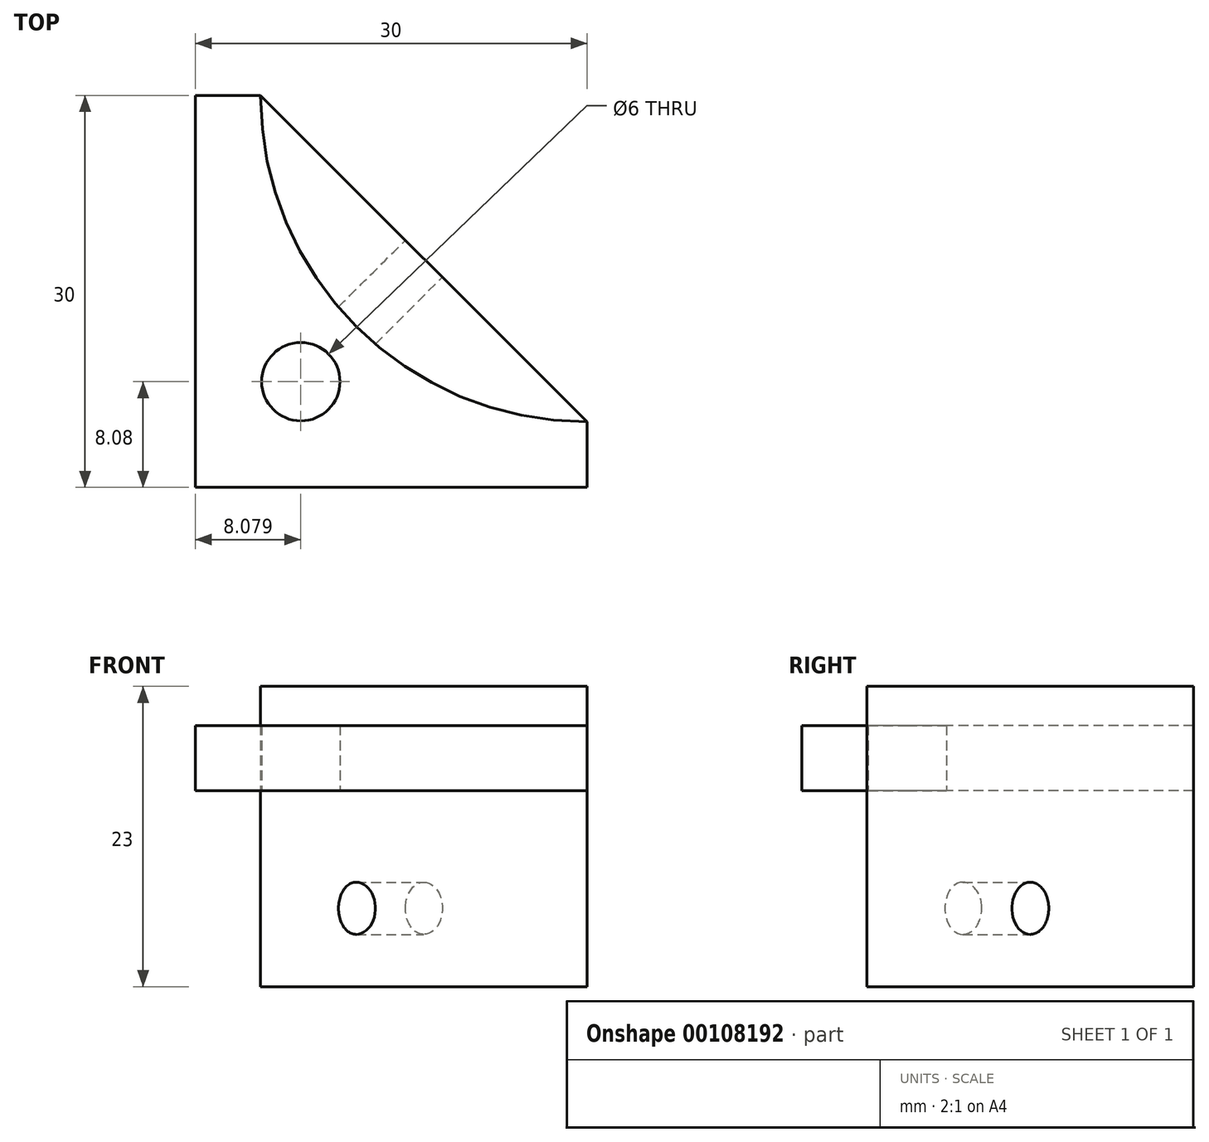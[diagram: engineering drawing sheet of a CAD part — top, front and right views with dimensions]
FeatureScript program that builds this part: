
annotation { "Feature Type Name" : "Feature", "Feature Type Description" : "" }
export const myFeature = defineFeature(function(context is Context, id is Id, definition is map)
    precondition{}
    {
        {
            var Q0;
            Q0=qCreatedBy(makeId("Top.planeOp"),FACE);
            var sketch = newSketch(context, id + "F0", { "sketchPlane" : qUnion([Q0])});
            skLineSegment(sketch, "E0.bottom", {"start": v(-30, 30) * mm, "end": v(30, 30) * mm});
            skLineSegment(sketch, "E0.top", {"start": v(-30, -30) * mm, "end": v(30, -30) * mm});
            skLineSegment(sketch, "E0.left", {"start": v(-30, 30) * mm, "end": v(-30, -30) * mm});
            skLineSegment(sketch, "E0.right", {"start": v(30, 30) * mm, "end": v(30, -30) * mm});
            skPoint(sketch, "E0.middle", {"position": v(0, 0) * mm});
            skCircle(sketch, "E1", {"center": v(0, 0) * mm, "radius": 25 * mm});
            skLineSegment(sketch, "E2", {"start": v(-30, 0) * mm, "end": v(-25, 0) * mm});
            skLineSegment(sketch, "E3", {"start": v(-25, 0) * mm, "end": v(0, -25) * mm});
            skLineSegment(sketch, "E4", {"start": v(0, -25) * mm, "end": v(0, -30) * mm});
            skCircle(sketch, "E5", {"center": v(-21.92, -21.92) * mm, "radius": 3 * mm});
            skSolve(sketch);
        }
        {
            var Q0;
            {var subQ0=sQuery(id+"F0.wireOp",EDGE,"E3");Q0=makeQuery(id+"F0.imprint","IMPRINT",FACE,{"disambiguationData":[TD([[makeQuery(id+"F0.imprint","IMPRINT",EDGE,{"derivedFrom":subQ0}),-1.0]])]});}
            extrude(context, id + "F1", {"entities" : qUnion([Q0]), "depth" : 8 * mm, "hasSecondDirection" : true, "secondDirectionOppositeDirection" : true, "secondDirectionDepth" : 15 * mm});
        }
        {
            var Q0;
            {var subQ0=sQuery(id+"F0.wireOp",EDGE,"E2");Q0=makeQuery(id+"F0.imprint","IMPRINT",FACE,{"disambiguationData":[TD([[makeQuery(id+"F0.imprint","IMPRINT",EDGE,{"derivedFrom":subQ0}),-1.0]])]});}
            extrude(context, id + "F2", {"entities" : qUnion([Q0]), "operationType" : NewBodyOperationType.ADD, "depth" : 5 * mm});
        }
        {
            var Q0;
            Q0=makeQuery(id+"F1.opExtrude","SWEPT_FACE",FACE,{"disambiguationData":[OSD([sQuery(id+"F0.wireOp",EDGE,"E3")])]});
            var sketch = newSketch(context, id + "F3", { "sketchPlane" : qUnion([Q0])});
            skCircle(sketch, "E6", {"center": v(0, -9) * mm, "radius": 2 * mm});
            skSolve(sketch);
        }
        {
            var Q0;
            Q0=makeQuery(id+"F3.imprint","IMPRINT",FACE,{"disambiguationData":[TD([[makeQuery(id+"F3.imprint","IMPRINT",EDGE,{"derivedFrom":sQuery(id+"F3.wireOp",EDGE,"E6")}),1.0]])]});
            var Q1;
            Q1=sQuery(id+"F3.wireOp",EDGE,"E6");
            extrude(context, id + "F4", {"entities" : qUnion([Q0]), "operationType" : NewBodyOperationType.REMOVE, "surfaceEntities" : qUnion([Q1]), "oppositeDirection" : true, "depth" : 25 * mm});
        }
    });
